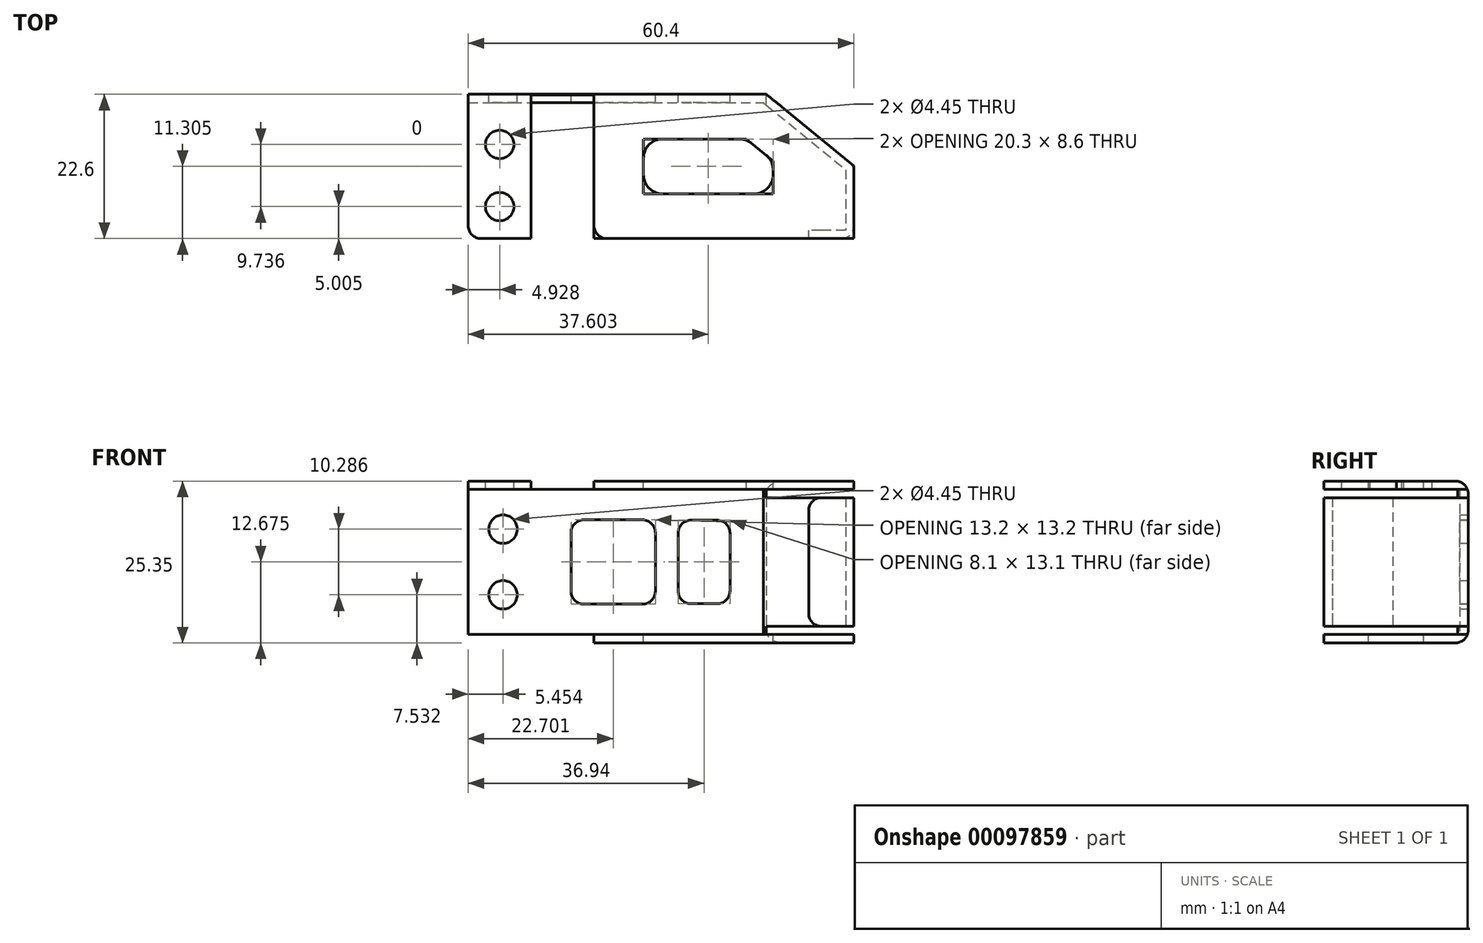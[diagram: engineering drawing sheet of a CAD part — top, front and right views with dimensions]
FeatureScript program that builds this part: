
annotation { "Feature Type Name" : "Feature", "Feature Type Description" : "" }
export const myFeature = defineFeature(function(context is Context, id is Id, definition is map)
    precondition{}
    {
        {
            var Q0;
            Q0=qCreatedBy(makeId("Top.planeOp"),FACE);
            var sketch = newSketch(context, id + "F0", { "sketchPlane" : qUnion([Q0])});
            skLineSegment(sketch, "E0.bottom", {"start": v(-31.59, -12.14) * mm, "end": v(13.31, -12.14) * mm});
            skLineSegment(sketch, "E0.top", {"start": v(-31.59, -33.44) * mm, "end": v(26.21, -33.44) * mm});
            skLineSegment(sketch, "E0.left", {"start": v(-31.59, -12.14) * mm, "end": v(-31.59, -33.44) * mm});
            skLineSegment(sketch, "E0.right", {"start": v(26.21, -22.66) * mm, "end": v(26.21, -33.44) * mm});
            skLineSegment(sketch, "E1", {"start": v(13.31, -12.14) * mm, "end": v(26.21, -22.66) * mm});
            skSolve(sketch);
        }
        {
            var Q0;
            Q0=makeQuery(id+"F0.imprint","IMPRINT",FACE,{"disambiguationData":[TD([[makeQuery(id+"F0.imprint","IMPRINT",EDGE,{"derivedFrom":sQuery(id+"F0.wireOp",EDGE,"E0.bottom")}),-1.0]])]});
            extrude(context, id + "F1", {"entities" : qUnion([Q0]), "depth" : 22.75 * mm});
        }
        {
            var Q0;
            Q0=makeQuery(id+"F1.opExtrude","SWEPT_FACE",FACE,{"disambiguationData":[OSD([sQuery(id+"F0.wireOp",EDGE,"E0.top")])]});
            shell(context, id + "F2", {"entities" : qUnion([Q0]), "thickness" : 1.3 * mm, "oppositeDirection" : true});
        }
        {
            var Q0;
            Q0=makeQuery(id+"F1.opExtrude","SWEPT_FACE",FACE,{"disambiguationData":[OSD([sQuery(id+"F0.wireOp",EDGE,"E0.left")])]});
            var sketch = newSketch(context, id + "F3", { "sketchPlane" : qUnion([Q0])});
            skLineSegment(sketch, "E2", {"start": v(12.14, -1.3) * mm, "end": v(12.14, 22.75) * mm});
            skLineSegment(sketch, "E3", {"start": v(12.14, 22.75) * mm, "end": v(33.44, 22.75) * mm});
            skSolve(sketch);
        }
        {
            var Q0;
            {var subQ0=sQuery(id+"F3.wireOp",EDGE,"E2");Q0=makeQuery(id+"F3.imprint","IMPRINT",FACE,{"disambiguationData":[TD([[makeQuery(id+"F3.imprint","IMPRINT",EDGE,{"derivedFrom":subQ0}),-1.0]])]});}
            extrude(context, id + "F4", {"entities" : qUnion([Q0]), "operationType" : NewBodyOperationType.REMOVE, "oppositeDirection" : true, "depth" : 19.7 * mm});
        }
        {
            var Q0;
            Q0=makeQuery(id+"F1.opExtrude","CAP_FACE",FACE,{"disambiguationData":[OSD([sQuery(id+"F0.wireOp",EDGE,"E0.bottom"),sQuery(id+"F0.wireOp",EDGE,"E0.top"),sQuery(id+"F0.wireOp",EDGE,"E0.left"),sQuery(id+"F0.wireOp",EDGE,"E0.right"),sQuery(id+"F0.wireOp",EDGE,"E1")])],"isStart":false});
            var sketch = newSketch(context, id + "F5", { "sketchPlane" : qUnion([Q0])});
            skLineSegment(sketch, "E4", {"start": v(-13.19, -12.14) * mm, "end": v(-13.19, -33.44) * mm});
            skLineSegment(sketch, "E5", {"start": v(-23.04, -33.44) * mm, "end": v(-23.04, -12.14) * mm});
            skLineSegment(sketch, "E6", {"start": v(-13.19, -33.44) * mm, "end": v(-32.89, -33.44) * mm});
            skLineSegment(sketch, "E7", {"start": v(-32.89, -33.44) * mm, "end": v(-23.04, -33.44) * mm});
            skLineSegment(sketch, "E8", {"start": v(-23.04, -12.14) * mm, "end": v(-32.89, -12.14) * mm});
            skLineSegment(sketch, "E9", {"start": v(-23.04, -12.14) * mm, "end": v(-23.04, -10.84) * mm});
            skLineSegment(sketch, "E10", {"start": v(-13.19, -12.14) * mm, "end": v(-13.19, -10.84) * mm});
            skSolve(sketch);
        }
        {
            var Q0;
            Q0=makeQuery(id+"F5.imprint","IMPRINT",FACE,{"disambiguationData":[TD([[makeQuery(id+"F5.imprint","IMPRINT",EDGE,{"derivedFrom":sQuery(id+"F5.wireOp",EDGE,"E4")}),-1.0]])]});
            extrude(context, id + "F6", {"entities" : qUnion([Q0]), "operationType" : NewBodyOperationType.REMOVE, "oppositeDirection" : true, "depth" : 1.3 * mm});
        }
        {
            var Q0;
            {var subQ0=sQuery(id+"F0.wireOp",EDGE,"E1");var subQ1=sQuery(id+"F0.wireOp",EDGE,"E0.top");var subQ2=sQuery(id+"F0.wireOp",EDGE,"E0.right");var subQ3=sQuery(id+"F0.wireOp",EDGE,"E0.bottom");Q0=makeQuery(id+"F6.boolean.opBoolean","SPLIT",FACE,{"disambiguationData":[TD([makeQuery(id+"F1.opExtrude","SWEPT_FACE",FACE,{"disambiguationData":[OSD([subQ2])]})])],"derivedFrom":makeQuery(id+"F1.opExtrude","CAP_FACE",FACE,{"disambiguationData":[OSD([subQ3,subQ1,sQuery(id+"F0.wireOp",EDGE,"E0.left"),subQ2,subQ0])],"isStart":false})});}
            var sketch = newSketch(context, id + "F7", { "sketchPlane" : qUnion([Q0])});
            skLineSegment(sketch, "E11", {"start": v(-5.44, -17.84) * mm, "end": v(10.65, -17.84) * mm});
            skLineSegment(sketch, "E12", {"start": v(10.65, -17.84) * mm, "end": v(14.86, -21.27) * mm});
            skLineSegment(sketch, "E13", {"start": v(14.86, -21.27) * mm, "end": v(14.86, -26.44) * mm});
            skLineSegment(sketch, "E14", {"start": v(14.86, -26.44) * mm, "end": v(-5.44, -26.44) * mm});
            skLineSegment(sketch, "E15", {"start": v(-5.44, -26.44) * mm, "end": v(-5.44, -17.84) * mm});
            skSolve(sketch);
        }
        {
            var Q0;
            Q0=makeQuery(id+"F7.imprint","IMPRINT",FACE,{"disambiguationData":[TD([[makeQuery(id+"F7.imprint","IMPRINT",EDGE,{"derivedFrom":sQuery(id+"F7.wireOp",EDGE,"E11")}),-1.0]])]});
            extrude(context, id + "F8", {"entities" : qUnion([Q0]), "operationType" : NewBodyOperationType.REMOVE, "oppositeDirection" : true, "depth" : 61.35 * mm});
        }
        {
            var Q0;
            Q0=makeQuery(id+"F1.opExtrude","SWEPT_FACE",FACE,{"disambiguationData":[OSD([sQuery(id+"F0.wireOp",EDGE,"E0.bottom")])]});
            var sketch = newSketch(context, id + "F9", { "sketchPlane" : qUnion([Q0])});
            skLineSegment(sketch, "E16.bottom", {"start": v(-8.1, 4.82) * mm, "end": v(0, 4.82) * mm});
            skLineSegment(sketch, "E16.top", {"start": v(-8.1, 17.93) * mm, "end": v(0, 17.93) * mm});
            skLineSegment(sketch, "E16.left", {"start": v(-8.1, 4.82) * mm, "end": v(-8.1, 17.93) * mm});
            skLineSegment(sketch, "E16.right", {"start": v(0, 4.82) * mm, "end": v(0, 17.93) * mm});
            skLineSegment(sketch, "E17.bottom", {"start": v(3.59, 4.77) * mm, "end": v(16.79, 4.77) * mm});
            skLineSegment(sketch, "E17.top", {"start": v(3.59, 17.97) * mm, "end": v(16.79, 17.97) * mm});
            skLineSegment(sketch, "E17.left", {"start": v(3.59, 4.77) * mm, "end": v(3.59, 17.98) * mm});
            skLineSegment(sketch, "E17.right", {"start": v(16.79, 4.77) * mm, "end": v(16.79, 17.97) * mm});
            skLineSegment(sketch, "E18", {"start": v(27.44, -1.3) * mm, "end": v(27.44, 24.05) * mm, "construction": true});
            skLineSegment(sketch, "E19", {"start": v(-13.78, 11.38) * mm, "end": v(32.89, 11.38) * mm, "construction": true});
            skCircle(sketch, "E20", {"center": v(27.44, 16.52) * mm, "radius": 2.23 * mm});
            skCircle(sketch, "E21", {"center": v(27.44, 6.23) * mm, "radius": 2.23 * mm});
            skLineSegment(sketch, "E22", {"start": v(27.44, 14.3) * mm, "end": v(27.44, 11.38) * mm});
            skLineSegment(sketch, "E23", {"start": v(27.44, 11.38) * mm, "end": v(27.44, 8.46) * mm});
            skLineSegment(sketch, "E24", {"start": v(13.19, -1.3) * mm, "end": v(13.19, 0) * mm});
            skLineSegment(sketch, "E25", {"start": v(13.19, 0) * mm, "end": v(32.89, 0) * mm});
            skPoint(sketch, "E26", {"position": v(16.79, 11.37) * mm});
            skPoint(sketch, "E27", {"position": v(0, 11.37) * mm});
            skSolve(sketch);
        }
        {
            var Q0;
            Q0=makeQuery(id+"F9.imprint","IMPRINT",FACE,{"disambiguationData":[TD([[makeQuery(id+"F9.imprint","IMPRINT",EDGE,{"derivedFrom":sQuery(id+"F9.wireOp",EDGE,"E16.bottom")}),1.0]])]});
            var Q1;
            Q1=makeQuery(id+"F9.imprint","IMPRINT",FACE,{"disambiguationData":[TD([[makeQuery(id+"F9.imprint","IMPRINT",EDGE,{"derivedFrom":sQuery(id+"F9.wireOp",EDGE,"E17.bottom")}),1.0]])]});
            var Q2;
            {var subQ0=sQuery(id+"F9.wireOp",EDGE,"E24");Q2=makeQuery(id+"F9.imprint","IMPRINT",FACE,{"disambiguationData":[TD([[makeQuery(id+"F9.imprint","IMPRINT",EDGE,{"derivedFrom":subQ0}),-1.0]])]});}
            var Q3;
            Q3=makeQuery(id+"F9.imprint","IMPRINT",FACE,{"disambiguationData":[TD([[makeQuery(id+"F9.imprint","IMPRINT",EDGE,{"derivedFrom":sQuery(id+"F9.wireOp",EDGE,"E21")}),1.0]])]});
            var Q4;
            Q4=makeQuery(id+"F9.imprint","IMPRINT",FACE,{"disambiguationData":[TD([[makeQuery(id+"F9.imprint","IMPRINT",EDGE,{"derivedFrom":sQuery(id+"F9.wireOp",EDGE,"E20")}),1.0]])]});
            extrude(context, id + "F10", {"entities" : qUnion([Q0, Q1, Q2, Q3, Q4]), "operationType" : NewBodyOperationType.REMOVE, "oppositeDirection" : true, "depth" : 25 * mm});
        }
        {
            var Q0;
            Q0=makeQuery(id+"F2.opShell","OFFSET_FACE",FACE,{"disambiguationData":[OSD([sQuery(id+"F0.wireOp",EDGE,"E0.right")])]});
            var sketch = newSketch(context, id + "F11", { "sketchPlane" : qUnion([Q0])});
            skLineSegment(sketch, "E28", {"start": v(32.14, 22.75) * mm, "end": v(32.14, 0) * mm});
            skSolve(sketch);
        }
        {
            var Q0;
            {var subQ0=sQuery(id+"F11.wireOp",EDGE,"E28");Q0=makeQuery(id+"F11.imprint","IMPRINT",FACE,{"disambiguationData":[TD([[makeQuery(id+"F11.imprint","IMPRINT",EDGE,{"derivedFrom":subQ0}),1.0]])]});}
            extrude(context, id + "F12", {"entities" : qUnion([Q0]), "operationType" : NewBodyOperationType.ADD, "depth" : 5.8 * mm});
        }
        {
            var Q0;
            Q0=makeQuery(id+"F1.opExtrude","SWEPT_FACE",FACE,{"disambiguationData":[OSD([sQuery(id+"F0.wireOp",EDGE,"E0.bottom")])]});
            var sketch = newSketch(context, id + "F13", { "sketchPlane" : qUnion([Q0])});
            skLineSegment(sketch, "E29", {"start": v(-13.78, 0) * mm, "end": v(-36.67, 0) * mm});
            skLineSegment(sketch, "E30", {"start": v(-13.78, 22.75) * mm, "end": v(-38.37, 22.75) * mm});
            skLineSegment(sketch, "E31", {"start": v(-13.78, 1.3) * mm, "end": v(-36.66, 1.3) * mm});
            skLineSegment(sketch, "E32", {"start": v(-13.78, 21.45) * mm, "end": v(-38.37, 21.45) * mm});
            skLineSegment(sketch, "E33", {"start": v(-36.67, 0) * mm, "end": v(-36.66, 1.3) * mm});
            skLineSegment(sketch, "E34", {"start": v(-38.37, 21.45) * mm, "end": v(-38.37, 22.75) * mm});
            skSolve(sketch);
        }
        {
            var Q0;
            {var subQ0=sQuery(id+"F13.wireOp",EDGE,"E29");Q0=makeQuery(id+"F13.imprint","IMPRINT",FACE,{"disambiguationData":[TD([[makeQuery(id+"F13.imprint","IMPRINT",EDGE,{"derivedFrom":subQ0}),-1.0]])]});}
            var Q1;
            {var subQ0=sQuery(id+"F13.wireOp",EDGE,"E30");Q1=makeQuery(id+"F13.imprint","IMPRINT",FACE,{"disambiguationData":[TD([[makeQuery(id+"F13.imprint","IMPRINT",EDGE,{"derivedFrom":subQ0}),1.0]])]});}
            extrude(context, id + "F14", {"entities" : qUnion([Q0, Q1]), "operationType" : NewBodyOperationType.REMOVE, "oppositeDirection" : true, "depth" : 25 * mm});
        }
        {
            var Q0;
            Q0=makeQuery(id+"F4.boolean.opBoolean","COPY",EDGE,{"derivedFrom":makeQuery(id+"F4.opExtrude","CAP_EDGE",EDGE,{"disambiguationData":[OSD([sQuery(id+"F0.wireOp",EDGE,"E0.top"),sQuery(id+"F0.wireOp",EDGE,"E0.left")])],"isStart":false})});
            var Q1;
            {var subQ0=sQuery(id+"F0.wireOp",EDGE,"E0.right");var subQ1=sQuery(id+"F0.wireOp",EDGE,"E0.top");Q1=makeQuery(id+"F14.boolean.opBoolean","SPLIT",EDGE,{"disambiguationData":[TD([makeQuery(id+"F14.opExtrude","SWEPT_FACE",FACE,{"disambiguationData":[OSD([sQuery(id+"F13.wireOp",EDGE,"E31")])]})])],"derivedFrom":makeQuery(id+"F1.opExtrude","SWEPT_EDGE",EDGE,{"disambiguationData":[OSD([subQ1,subQ0])]})});}
            var Q2;
            {var subQ1=sQuery(id+"F0.wireOp",EDGE,"E0.right");var subQ3=sQuery(id+"F0.wireOp",EDGE,"E0.top");Q2=makeQuery(id+"F14.boolean.opBoolean","SPLIT",EDGE,{"disambiguationData":[TD([makeQuery(id+"F14.opExtrude","SWEPT_FACE",FACE,{"disambiguationData":[OSD([sQuery(id+"F13.wireOp",EDGE,"E29")])]})])],"derivedFrom":makeQuery(id+"F1.opExtrude","SWEPT_EDGE",EDGE,{"disambiguationData":[OSD([subQ3,subQ1])]})});}
            var Q3;
            {var subQ1=sQuery(id+"F0.wireOp",EDGE,"E0.right");var subQ3=sQuery(id+"F0.wireOp",EDGE,"E0.top");Q3=makeQuery(id+"F14.boolean.opBoolean","SPLIT",EDGE,{"disambiguationData":[TD([makeQuery(id+"F4.opExtrude","SWEPT_FACE",FACE,{"disambiguationData":[OSD([sQuery(id+"F3.wireOp",EDGE,"E3")])]})])],"derivedFrom":makeQuery(id+"F1.opExtrude","SWEPT_EDGE",EDGE,{"disambiguationData":[OSD([subQ3,subQ1])]})});}
            var Q4;
            Q4=makeQuery(id+"F6.boolean.opBoolean","COPY",EDGE,{"derivedFrom":makeQuery(id+"F6.opExtrude","SWEPT_EDGE",EDGE,{"disambiguationData":[OSD([sQuery(id+"F0.wireOp",EDGE,"E0.top"),sQuery(id+"F5.wireOp",EDGE,"E4"),sQuery(id+"F5.wireOp",EDGE,"E6")])]})});
            var Q5;
            Q5=makeQuery(id+"F1.opExtrude","SWEPT_EDGE",EDGE,{"disambiguationData":[OSD([sQuery(id+"F0.wireOp",EDGE,"E0.top"),sQuery(id+"F0.wireOp",EDGE,"E0.left")])]});
            var Q6;
            Q6=makeQuery(id+"F6.boolean.opBoolean","COPY",EDGE,{"derivedFrom":makeQuery(id+"F6.opExtrude","SWEPT_EDGE",EDGE,{"disambiguationData":[OSD([sQuery(id+"F5.wireOp",EDGE,"E5"),sQuery(id+"F5.wireOp",EDGE,"E6"),sQuery(id+"F5.wireOp",EDGE,"E7")])]})});
            var Q7;
            Q7=makeQuery(id+"F10.boolean.opBoolean","COPY",EDGE,{"derivedFrom":makeQuery(id+"F10.opExtrude","SWEPT_EDGE",EDGE,{"disambiguationData":[OSD([sQuery(id+"F0.wireOp",EDGE,"E0.bottom"),sQuery(id+"F0.wireOp",EDGE,"E0.left"),sQuery(id+"F9.wireOp",EDGE,"E25")])]})});
            var Q8;
            Q8=makeQuery(id+"F14.boolean.opBoolean","INTERSECT",EDGE,{"derivedFrom":[makeQuery(id+"F12.opExtrude","CAP_FACE",FACE,{"disambiguationData":[OSD([sQuery(id+"F0.wireOp",EDGE,"E0.top"),sQuery(id+"F0.wireOp",EDGE,"E0.right"),sQuery(id+"F11.wireOp",EDGE,"E28")])],"isStart":false}),makeQuery(id+"F14.opExtrude","SWEPT_FACE",FACE,{"disambiguationData":[OSD([sQuery(id+"F13.wireOp",EDGE,"E31")])]})]});
            var Q9;
            Q9=makeQuery(id+"F14.boolean.opBoolean","INTERSECT",EDGE,{"derivedFrom":[makeQuery(id+"F12.opExtrude","CAP_FACE",FACE,{"disambiguationData":[OSD([sQuery(id+"F0.wireOp",EDGE,"E0.top"),sQuery(id+"F0.wireOp",EDGE,"E0.right"),sQuery(id+"F11.wireOp",EDGE,"E28")])],"isStart":false}),makeQuery(id+"F14.opExtrude","SWEPT_FACE",FACE,{"disambiguationData":[OSD([sQuery(id+"F13.wireOp",EDGE,"E32")])]})]});
            fillet(context, id + "F15", {"entities" : qUnion([Q0, Q1, Q2, Q3, Q4, Q5, Q6, Q7, Q8, Q9]), "radius" : 2 * mm, "tangentPropagation" : true, "allowEdgeOverflow" : false});
        }
        {
            var Q0;
            {var subQ0=sQuery(id+"F0.wireOp",EDGE,"E1");var subQ1=sQuery(id+"F0.wireOp",EDGE,"E0.right");var subQ2=sQuery(id+"F0.wireOp",EDGE,"E0.left");var subQ3=sQuery(id+"F0.wireOp",EDGE,"E0.top");var subQ4=sQuery(id+"F0.wireOp",EDGE,"E0.bottom");var subQ5=makeQuery(id+"F1.opExtrude","CAP_FACE",FACE,{"disambiguationData":[OSD([subQ4,subQ3,subQ2,subQ1,subQ0])],"isStart":true});var subQ6=sQuery(id+"F7.wireOp",EDGE,"E13");var subQ7=sQuery(id+"F7.wireOp",EDGE,"E12");Q0=makeQuery(id+"F8.boolean.opBoolean","COPY",EDGE,{"disambiguationData":[TD([subQ5])],"derivedFrom":makeQuery(id+"F8.opExtrude","SWEPT_EDGE",EDGE,{"disambiguationData":[OSD([subQ7,subQ6])]})});}
            var Q1;
            {var subQ0=sQuery(id+"F0.wireOp",EDGE,"E1");var subQ1=sQuery(id+"F0.wireOp",EDGE,"E0.right");var subQ2=sQuery(id+"F0.wireOp",EDGE,"E0.left");var subQ3=sQuery(id+"F0.wireOp",EDGE,"E0.top");var subQ4=sQuery(id+"F0.wireOp",EDGE,"E0.bottom");var subQ5=makeQuery(id+"F1.opExtrude","CAP_FACE",FACE,{"disambiguationData":[OSD([subQ4,subQ3,subQ2,subQ1,subQ0])],"isStart":true});var subQ6=sQuery(id+"F7.wireOp",EDGE,"E11");var subQ7=sQuery(id+"F7.wireOp",EDGE,"E12");Q1=makeQuery(id+"F8.boolean.opBoolean","COPY",EDGE,{"disambiguationData":[TD([subQ5])],"derivedFrom":makeQuery(id+"F8.opExtrude","SWEPT_EDGE",EDGE,{"disambiguationData":[OSD([subQ6,subQ7])]})});}
            var Q2;
            {var subQ0=sQuery(id+"F0.wireOp",EDGE,"E1");var subQ1=sQuery(id+"F0.wireOp",EDGE,"E0.right");var subQ2=sQuery(id+"F0.wireOp",EDGE,"E0.left");var subQ3=sQuery(id+"F0.wireOp",EDGE,"E0.top");var subQ4=sQuery(id+"F0.wireOp",EDGE,"E0.bottom");var subQ5=makeQuery(id+"F1.opExtrude","CAP_FACE",FACE,{"disambiguationData":[OSD([subQ4,subQ3,subQ2,subQ1,subQ0])],"isStart":true});var subQ6=sQuery(id+"F7.wireOp",EDGE,"E11");var subQ7=sQuery(id+"F7.wireOp",EDGE,"E15");Q2=makeQuery(id+"F8.boolean.opBoolean","COPY",EDGE,{"disambiguationData":[TD([subQ5])],"derivedFrom":makeQuery(id+"F8.opExtrude","SWEPT_EDGE",EDGE,{"disambiguationData":[OSD([subQ6,subQ7])]})});}
            var Q3;
            {var subQ0=sQuery(id+"F0.wireOp",EDGE,"E1");var subQ1=sQuery(id+"F0.wireOp",EDGE,"E0.right");var subQ2=sQuery(id+"F0.wireOp",EDGE,"E0.left");var subQ3=sQuery(id+"F0.wireOp",EDGE,"E0.top");var subQ4=sQuery(id+"F0.wireOp",EDGE,"E0.bottom");var subQ5=makeQuery(id+"F1.opExtrude","CAP_FACE",FACE,{"disambiguationData":[OSD([subQ4,subQ3,subQ2,subQ1,subQ0])],"isStart":true});var subQ6=sQuery(id+"F7.wireOp",EDGE,"E14");var subQ7=sQuery(id+"F7.wireOp",EDGE,"E15");Q3=makeQuery(id+"F8.boolean.opBoolean","COPY",EDGE,{"disambiguationData":[TD([subQ5])],"derivedFrom":makeQuery(id+"F8.opExtrude","SWEPT_EDGE",EDGE,{"disambiguationData":[OSD([subQ6,subQ7])]})});}
            var Q4;
            {var subQ0=sQuery(id+"F0.wireOp",EDGE,"E1");var subQ1=sQuery(id+"F0.wireOp",EDGE,"E0.right");var subQ2=sQuery(id+"F0.wireOp",EDGE,"E0.left");var subQ3=sQuery(id+"F0.wireOp",EDGE,"E0.top");var subQ4=sQuery(id+"F0.wireOp",EDGE,"E0.bottom");var subQ5=makeQuery(id+"F1.opExtrude","CAP_FACE",FACE,{"disambiguationData":[OSD([subQ4,subQ3,subQ2,subQ1,subQ0])],"isStart":true});var subQ6=sQuery(id+"F7.wireOp",EDGE,"E13");var subQ7=sQuery(id+"F7.wireOp",EDGE,"E14");Q4=makeQuery(id+"F8.boolean.opBoolean","COPY",EDGE,{"disambiguationData":[TD([subQ5])],"derivedFrom":makeQuery(id+"F8.opExtrude","SWEPT_EDGE",EDGE,{"disambiguationData":[OSD([subQ6,subQ7])]})});}
            var Q5;
            {var subQ0=sQuery(id+"F7.wireOp",EDGE,"E11");var subQ7=sQuery(id+"F7.wireOp",EDGE,"E12");Q5=makeQuery(id+"F8.boolean.opBoolean","COPY",EDGE,{"disambiguationData":[TD([makeQuery(id+"F4.opExtrude","SWEPT_FACE",FACE,{"disambiguationData":[OSD([sQuery(id+"F3.wireOp",EDGE,"E3")])]})])],"derivedFrom":makeQuery(id+"F8.opExtrude","SWEPT_EDGE",EDGE,{"disambiguationData":[OSD([subQ0,subQ7])]})});}
            var Q6;
            {var subQ0=sQuery(id+"F7.wireOp",EDGE,"E12");var subQ7=sQuery(id+"F7.wireOp",EDGE,"E13");Q6=makeQuery(id+"F8.boolean.opBoolean","COPY",EDGE,{"disambiguationData":[TD([makeQuery(id+"F4.opExtrude","SWEPT_FACE",FACE,{"disambiguationData":[OSD([sQuery(id+"F3.wireOp",EDGE,"E3")])]})])],"derivedFrom":makeQuery(id+"F8.opExtrude","SWEPT_EDGE",EDGE,{"disambiguationData":[OSD([subQ0,subQ7])]})});}
            var Q7;
            {var subQ0=sQuery(id+"F7.wireOp",EDGE,"E13");var subQ7=sQuery(id+"F7.wireOp",EDGE,"E14");Q7=makeQuery(id+"F8.boolean.opBoolean","COPY",EDGE,{"disambiguationData":[TD([makeQuery(id+"F4.opExtrude","SWEPT_FACE",FACE,{"disambiguationData":[OSD([sQuery(id+"F3.wireOp",EDGE,"E3")])]})])],"derivedFrom":makeQuery(id+"F8.opExtrude","SWEPT_EDGE",EDGE,{"disambiguationData":[OSD([subQ0,subQ7])]})});}
            var Q8;
            {var subQ0=sQuery(id+"F7.wireOp",EDGE,"E14");var subQ7=sQuery(id+"F7.wireOp",EDGE,"E15");Q8=makeQuery(id+"F8.boolean.opBoolean","COPY",EDGE,{"disambiguationData":[TD([makeQuery(id+"F4.opExtrude","SWEPT_FACE",FACE,{"disambiguationData":[OSD([sQuery(id+"F3.wireOp",EDGE,"E3")])]})])],"derivedFrom":makeQuery(id+"F8.opExtrude","SWEPT_EDGE",EDGE,{"disambiguationData":[OSD([subQ0,subQ7])]})});}
            var Q9;
            {var subQ0=sQuery(id+"F7.wireOp",EDGE,"E11");var subQ7=sQuery(id+"F7.wireOp",EDGE,"E15");Q9=makeQuery(id+"F8.boolean.opBoolean","COPY",EDGE,{"disambiguationData":[TD([makeQuery(id+"F4.opExtrude","SWEPT_FACE",FACE,{"disambiguationData":[OSD([sQuery(id+"F3.wireOp",EDGE,"E3")])]})])],"derivedFrom":makeQuery(id+"F8.opExtrude","SWEPT_EDGE",EDGE,{"disambiguationData":[OSD([subQ0,subQ7])]})});}
            fillet(context, id + "F16", {"entities" : qUnion([Q0, Q1, Q2, Q3, Q4, Q5, Q6, Q7, Q8, Q9]), "radius" : 3 * mm, "tangentPropagation" : true, "allowEdgeOverflow" : false});
        }
        {
            var Q0;
            {var subQ0=sQuery(id+"F0.wireOp",EDGE,"E0.bottom");var subQ1=sQuery(id+"F0.wireOp",EDGE,"E1");Q0=makeQuery(id+"F6.boolean.opBoolean","SPLIT",EDGE,{"disambiguationData":[TD([makeQuery(id+"F1.opExtrude","SWEPT_FACE",FACE,{"disambiguationData":[OSD([subQ1])]})])],"derivedFrom":makeQuery(id+"F1.opExtrude","CAP_EDGE",EDGE,{"disambiguationData":[OSD([subQ0])],"isStart":false})});}
            var Q1;
            {var subQ0=sQuery(id+"F0.wireOp",EDGE,"E0.bottom");var subQ1=sQuery(id+"F0.wireOp",EDGE,"E0.left");Q1=makeQuery(id+"F6.boolean.opBoolean","SPLIT",EDGE,{"disambiguationData":[TD([makeQuery(id+"F1.opExtrude","SWEPT_FACE",FACE,{"disambiguationData":[OSD([subQ1])]})])],"derivedFrom":makeQuery(id+"F1.opExtrude","CAP_EDGE",EDGE,{"disambiguationData":[OSD([subQ0])],"isStart":false})});}
            var Q2;
            Q2=makeQuery(id+"F1.opExtrude","CAP_EDGE",EDGE,{"disambiguationData":[OSD([sQuery(id+"F0.wireOp",EDGE,"E0.bottom")])],"isStart":true});
            var Q3;
            {var subQ0=sQuery(id+"F0.wireOp",EDGE,"E0.right");var subQ1=sQuery(id+"F0.wireOp",EDGE,"E1");Q3=makeQuery(id+"F14.boolean.opBoolean","SPLIT",EDGE,{"disambiguationData":[TD([makeQuery(id+"F14.opExtrude","SWEPT_FACE",FACE,{"disambiguationData":[OSD([sQuery(id+"F13.wireOp",EDGE,"E31")])]})])],"derivedFrom":makeQuery(id+"F1.opExtrude","SWEPT_EDGE",EDGE,{"disambiguationData":[OSD([subQ0,subQ1])]})});}
            var Q4;
            {var subQ0=sQuery(id+"F0.wireOp",EDGE,"E1");var subQ1=sQuery(id+"F0.wireOp",EDGE,"E0.right");Q4=makeQuery(id+"F14.boolean.opBoolean","SPLIT",EDGE,{"disambiguationData":[TD([makeQuery(id+"F4.opExtrude","SWEPT_FACE",FACE,{"disambiguationData":[OSD([sQuery(id+"F3.wireOp",EDGE,"E3")])]})])],"derivedFrom":makeQuery(id+"F1.opExtrude","SWEPT_EDGE",EDGE,{"disambiguationData":[OSD([subQ1,subQ0])]})});}
            var Q5;
            {var subQ0=sQuery(id+"F0.wireOp",EDGE,"E1");var subQ1=sQuery(id+"F0.wireOp",EDGE,"E0.right");Q5=makeQuery(id+"F14.boolean.opBoolean","SPLIT",EDGE,{"disambiguationData":[TD([makeQuery(id+"F14.opExtrude","SWEPT_FACE",FACE,{"disambiguationData":[OSD([sQuery(id+"F13.wireOp",EDGE,"E29")])]})])],"derivedFrom":makeQuery(id+"F1.opExtrude","SWEPT_EDGE",EDGE,{"disambiguationData":[OSD([subQ1,subQ0])]})});}
            fillet(context, id + "F17", {"entities" : qUnion([Q0, Q1, Q2, Q3, Q4, Q5]), "radius" : 2 * mm, "tangentPropagation" : true, "allowEdgeOverflow" : false});
        }
        {
            var Q0;
            Q0=makeQuery(id+"F10.boolean.opBoolean","COPY",EDGE,{"derivedFrom":makeQuery(id+"F10.opExtrude","SWEPT_EDGE",EDGE,{"disambiguationData":[OSD([sQuery(id+"F9.wireOp",EDGE,"E16.top"),sQuery(id+"F9.wireOp",EDGE,"E16.right")])]})});
            var Q1;
            Q1=makeQuery(id+"F10.boolean.opBoolean","COPY",EDGE,{"derivedFrom":makeQuery(id+"F10.opExtrude","SWEPT_EDGE",EDGE,{"disambiguationData":[OSD([sQuery(id+"F9.wireOp",EDGE,"E16.bottom"),sQuery(id+"F9.wireOp",EDGE,"E16.right")])]})});
            var Q2;
            Q2=makeQuery(id+"F10.boolean.opBoolean","COPY",EDGE,{"derivedFrom":makeQuery(id+"F10.opExtrude","SWEPT_EDGE",EDGE,{"disambiguationData":[OSD([sQuery(id+"F9.wireOp",EDGE,"E16.bottom"),sQuery(id+"F9.wireOp",EDGE,"E16.left")])]})});
            var Q3;
            Q3=makeQuery(id+"F10.boolean.opBoolean","COPY",EDGE,{"derivedFrom":makeQuery(id+"F10.opExtrude","SWEPT_EDGE",EDGE,{"disambiguationData":[OSD([sQuery(id+"F9.wireOp",EDGE,"E16.top"),sQuery(id+"F9.wireOp",EDGE,"E16.left")])]})});
            var Q4;
            Q4=makeQuery(id+"F10.boolean.opBoolean","COPY",EDGE,{"derivedFrom":makeQuery(id+"F10.opExtrude","SWEPT_EDGE",EDGE,{"disambiguationData":[OSD([sQuery(id+"F9.wireOp",EDGE,"E17.bottom"),sQuery(id+"F9.wireOp",EDGE,"E17.right")])]})});
            var Q5;
            Q5=makeQuery(id+"F10.boolean.opBoolean","COPY",EDGE,{"derivedFrom":makeQuery(id+"F10.opExtrude","SWEPT_EDGE",EDGE,{"disambiguationData":[OSD([sQuery(id+"F9.wireOp",EDGE,"E17.top"),sQuery(id+"F9.wireOp",EDGE,"E17.right")])]})});
            var Q6;
            Q6=makeQuery(id+"F10.boolean.opBoolean","COPY",EDGE,{"derivedFrom":makeQuery(id+"F10.opExtrude","SWEPT_EDGE",EDGE,{"disambiguationData":[OSD([sQuery(id+"F9.wireOp",EDGE,"E17.top"),sQuery(id+"F9.wireOp",EDGE,"E17.left")])]})});
            var Q7;
            Q7=makeQuery(id+"F10.boolean.opBoolean","COPY",EDGE,{"derivedFrom":makeQuery(id+"F10.opExtrude","SWEPT_EDGE",EDGE,{"disambiguationData":[OSD([sQuery(id+"F9.wireOp",EDGE,"E17.bottom"),sQuery(id+"F9.wireOp",EDGE,"E17.left")])]})});
            fillet(context, id + "F18", {"entities" : qUnion([Q0, Q1, Q2, Q3, Q4, Q5, Q6, Q7]), "radius" : 2 * mm, "tangentPropagation" : true, "allowEdgeOverflow" : false});
        }
        {
            var Q0;
            {var subQ0=sQuery(id+"F0.wireOp",EDGE,"E0.bottom");var subQ1=sQuery(id+"F0.wireOp",EDGE,"E0.top");var subQ2=sQuery(id+"F0.wireOp",EDGE,"E0.left");Q0=makeQuery(id+"F6.boolean.opBoolean","SPLIT",FACE,{"disambiguationData":[TD([makeQuery(id+"F1.opExtrude","SWEPT_FACE",FACE,{"disambiguationData":[OSD([subQ2])]})])],"derivedFrom":makeQuery(id+"F1.opExtrude","CAP_FACE",FACE,{"disambiguationData":[OSD([subQ0,subQ1,subQ2,sQuery(id+"F0.wireOp",EDGE,"E0.right"),sQuery(id+"F0.wireOp",EDGE,"E1")])],"isStart":false})});}
            var sketch = newSketch(context, id + "F19", { "sketchPlane" : qUnion([Q0])});
            skCircle(sketch, "E35", {"center": v(-27.96, -18.7) * mm, "radius": 2.23 * mm});
            skCircle(sketch, "E36", {"center": v(-27.96, -28.44) * mm, "radius": 2.23 * mm});
            skLineSegment(sketch, "E37", {"start": v(-27.96, -12.84) * mm, "end": v(-27.96, -33.44) * mm, "construction": true});
            skSolve(sketch);
        }
        {
            var Q0;
            Q0 = qSketchRegion(id + "F19", true);
            extrude(context, id + "F20", {"entities" : qUnion([Q0]), "operationType" : NewBodyOperationType.REMOVE, "oppositeDirection" : true, "depth" : 25 * mm});
        }
    });
